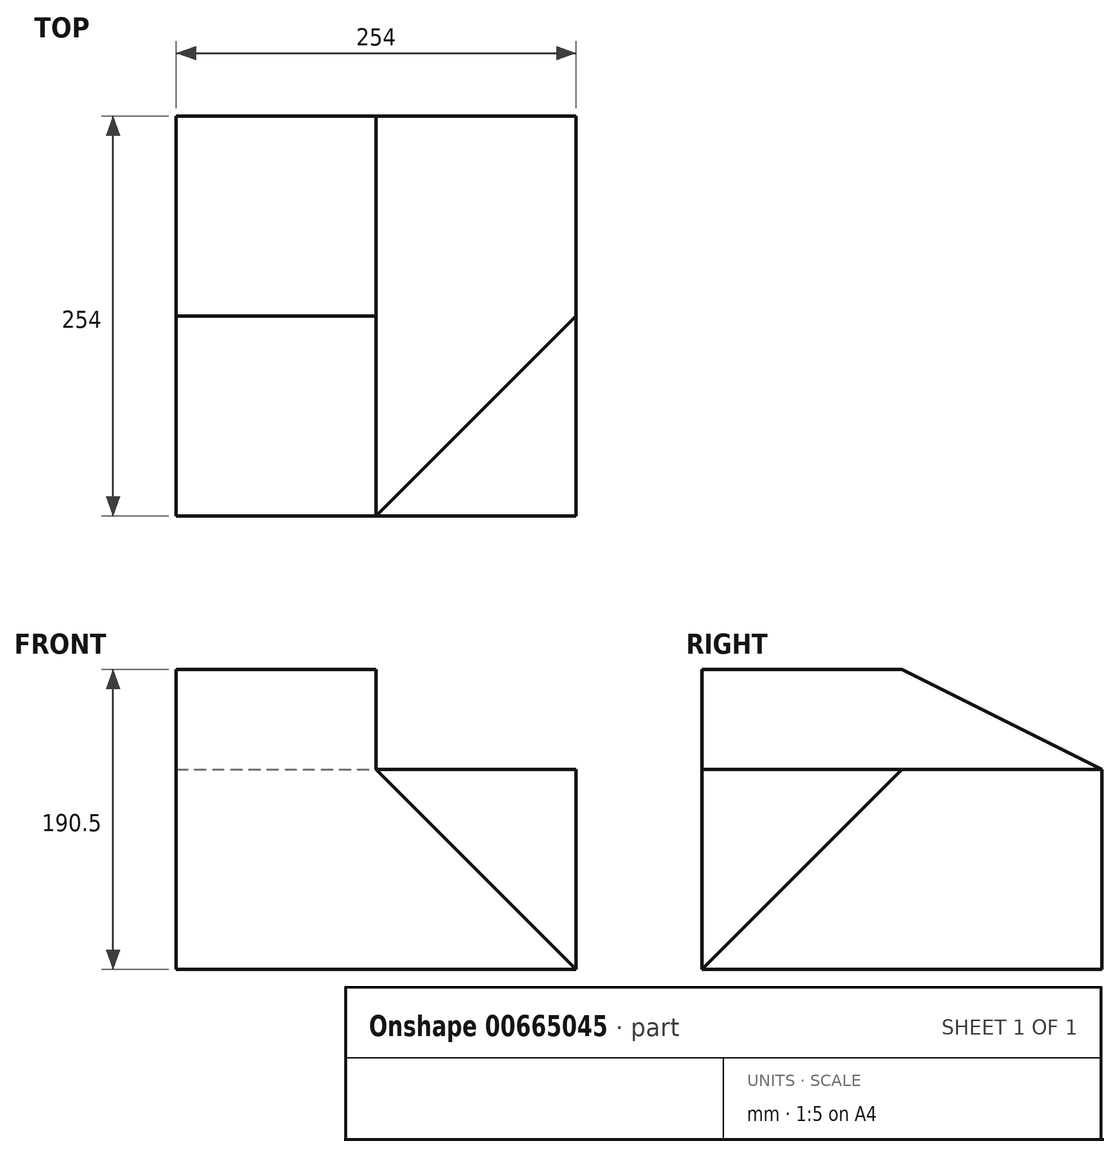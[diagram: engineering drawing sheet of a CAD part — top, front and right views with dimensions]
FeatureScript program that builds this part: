
annotation { "Feature Type Name" : "Feature", "Feature Type Description" : "" }
export const myFeature = defineFeature(function(context is Context, id is Id, definition is map)
    precondition{}
    {
        {
            var Q0;
            Q0=qCreatedBy(makeId("Front.planeOp"),FACE);
            var sketch = newSketch(context, id + "F0", { "sketchPlane" : qUnion([Q0])});
            skPoint(sketch, "E0.middle", {"position": v(0, 0) * mm});
            skLineSegment(sketch, "E1", {"start": v(0, 0) * mm, "end": v(254, 0) * mm});
            skLineSegment(sketch, "E2", {"start": v(254, 0) * mm, "end": v(254, 127) * mm});
            skLineSegment(sketch, "E3", {"start": v(254, 127) * mm, "end": v(127, 127) * mm});
            skLineSegment(sketch, "E4", {"start": v(127, 127) * mm, "end": v(127, 190.5) * mm});
            skLineSegment(sketch, "E5", {"start": v(127, 190.5) * mm, "end": v(0, 190.5) * mm});
            skLineSegment(sketch, "E6", {"start": v(0, 190.5) * mm, "end": v(0, 0) * mm});
            skSolve(sketch);
        }
        {
            var Q0;
            Q0=makeQuery(id+"F0.imprint","IMPRINT",FACE,{"disambiguationData":[TD([[makeQuery(id+"F0.imprint","IMPRINT",EDGE,{"derivedFrom":sQuery(id+"F0.wireOp",EDGE,"E1")}),1.0]])]});
            extrude(context, id + "F1", {"entities" : qUnion([Q0]), "endBound" : BoundingType.SYMMETRIC, "depth" : 254 * mm, "offsetDistance" : 25.4 * mm});
        }
        {
            var Q0;
            Q0=makeQuery(id+"F1.opExtrude","SWEPT_FACE",FACE,{"disambiguationData":[OSD([sQuery(id+"F0.wireOp",EDGE,"E4")])]});
            var sketch = newSketch(context, id + "F2", { "sketchPlane" : qUnion([Q0])});
            skLineSegment(sketch, "E7", {"start": v(0, 190.5) * mm, "end": v(127, 127) * mm});
            skSolve(sketch);
        }
        {
            var Q0;
            {var subQ0=sQuery(id+"F2.wireOp",EDGE,"E7");Q0=makeQuery(id+"F2.imprint","IMPRINT",FACE,{"disambiguationData":[TD([[makeQuery(id+"F2.imprint","IMPRINT",EDGE,{"derivedFrom":subQ0}),1.0]])]});}
            extrude(context, id + "F3", {"entities" : qUnion([Q0]), "operationType" : NewBodyOperationType.REMOVE, "oppositeDirection" : true, "depth" : 127 * mm, "offsetDistance" : 25.4 * mm});
        }
        {
            var Q0;
            Q0=makeQuery(id+"F1.opExtrude","SWEPT_EDGE",EDGE,{"disambiguationData":[OSD([sQuery(id+"F0.wireOp",EDGE,"E2"),sQuery(id+"F0.wireOp",EDGE,"E3")])]});
            cPoint(context, id + "F4", {"entities" : qUnion([Q0]), "parameter" : 0.5});
        }
        {
            var Q0;
            Q0=makeQuery(id+"F1.opExtrude","CAP_VERTEX",VERTEX,{"disambiguationData":[OSD([sQuery(id+"F0.wireOp",EDGE,"E3"),sQuery(id+"F0.wireOp",EDGE,"E4")])],"isStart":false});
            var Q1;
            Q1 = qCreatedBy(id + "F4" ,VERTEX);
            var Q2;
            Q2=makeQuery(id+"F1.opExtrude","CAP_VERTEX",VERTEX,{"disambiguationData":[OSD([sQuery(id+"F0.wireOp",EDGE,"E1"),sQuery(id+"F0.wireOp",EDGE,"E2")])],"isStart":false});
            cPlane(context, id + "F5", {"entities" : qUnion([Q0, Q1, Q2]), "cplaneType" : CPlaneType.THREE_POINT, "offset" : 25.4 * mm, "width" : 152.4 * mm, "height" : 152.4 * mm});
        }
        {
            var Q0;
            Q0=qCreatedBy(id+"F5.planeOp",FACE);
            var sketch = newSketch(context, id + "F6", { "sketchPlane" : qUnion([Q0])});
            skLineSegment(sketch, "E8", {"start": v(0, 0) * mm, "end": v(155.54, 89.8) * mm});
            skLineSegment(sketch, "E9", {"start": v(155.54, 89.8) * mm, "end": v(155.54, -89.8) * mm});
            skLineSegment(sketch, "E10", {"start": v(0, 0) * mm, "end": v(155.54, -89.8) * mm});
            skSolve(sketch);
        }
        {
            var Q0;
            Q0 = qSketchRegion(id + "F6", true);
            extrude(context, id + "F7", {"entities" : qUnion([Q0]), "operationType" : NewBodyOperationType.REMOVE, "depth" : 246.89 * mm, "offsetDistance" : 25.4 * mm});
        }
    });
